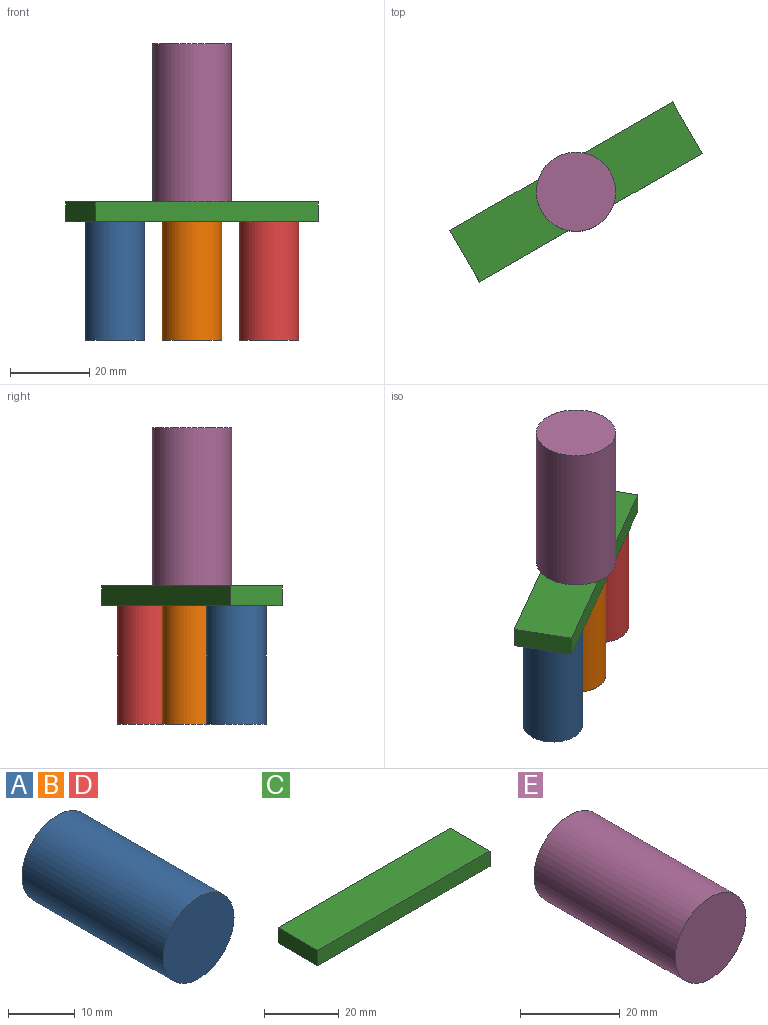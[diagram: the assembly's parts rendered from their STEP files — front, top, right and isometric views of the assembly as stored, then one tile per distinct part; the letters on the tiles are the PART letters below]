
ASSEMBLY  parts=5 mates=4
PART A: 3 faces, bbox 15x30x15 mm
  f0: cylinder r=7.5mm len=30mm, axis (0,1,0), area 1413.7mm2, adj f1,f2
  f1: plane 15x15mm, normal (0,-1,0), area 176.7mm2, adj f0
  f2: plane 15x15mm, normal (0,1,0), area 176.7mm2, adj f0
PART B: same geometry as A
PART C: 6 faces, bbox 65x15x5 mm
  f0: plane 15x5mm, normal (-1,0,0), area 75mm2, adj f1,f3,f4,f5
  f1: plane 65x15mm, normal (0,0,-1), area 975mm2, adj f0,f2,f4,f5
  f2: plane 15x5mm, normal (1,0,0), area 75mm2, adj f1,f3,f4,f5
  f3: plane 65x15mm, normal (0,0,1), area 975mm2, adj f0,f2,f4,f5
  f4: plane 65x5mm, normal (0,-1,0), area 325mm2, adj f0,f1,f2,f3
  f5: plane 65x5mm, normal (0,1,0), area 325mm2, adj f0,f1,f2,f3
PART D: same geometry as A
PART E: 3 faces, bbox 20x40x20 mm
  f0: cylinder r=10mm len=40mm, axis (0,1,0), area 2513.3mm2, adj f1,f2
  f1: plane 20x20mm, normal (0,-1,0), area 314.2mm2, adj f0
  f2: plane 20x20mm, normal (0,1,0), area 314.2mm2, adj f0
PLACE A rot(axis=(0.94,0.25,0.25),93.8deg) t=(-37.86,40.12,4.43)mm
PLACE B rot(axis=(0.94,0.25,0.25),93.8deg) t=(-18.37,51.37,4.43)mm
PLACE C rot(axis=(0,0,1),30deg) t=(-62.24,-13.62,46.84)mm
PLACE D rot(axis=(0.94,0.25,0.25),93.8deg) t=(1.11,62.62,4.43)mm
PLACE E rot(axis=(0.19,-0.69,-0.69),158.9deg) t=(-51.73,-16.21,49.43)mm
MATE fastened A.f0 <-> C.f1  axis (0,0,1) through (-71.22,-27.46,4.43)mm
MATE fastened D.f0 <-> C.f1  axis (0,0,1) through (-32.25,-4.96,4.43)mm
MATE fastened E.f0 <-> C.f3  axis (0,0,-1) through (-51.73,-16.21,9.43)mm
MATE fastened B.f0 <-> C.f1  axis (0,0,1) through (-51.73,-16.21,4.43)mm
